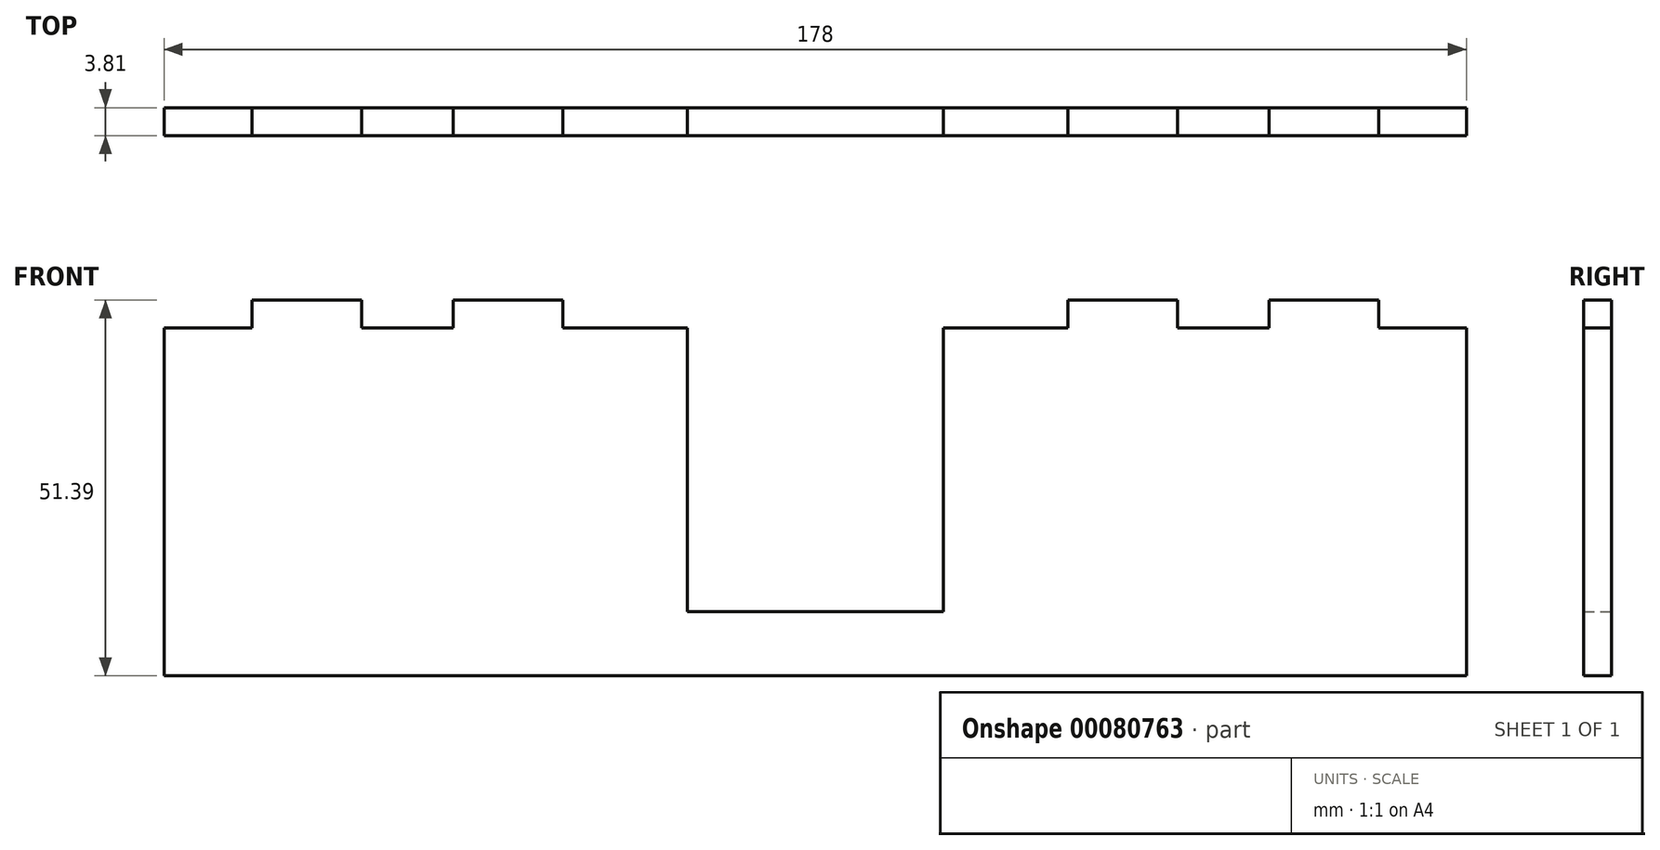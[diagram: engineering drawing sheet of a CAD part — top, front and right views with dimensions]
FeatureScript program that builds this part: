
annotation { "Feature Type Name" : "Feature", "Feature Type Description" : "" }
export const myFeature = defineFeature(function(context is Context, id is Id, definition is map)
    precondition{}
    {
        {
            var Q0;
            Q0=qCreatedBy(makeId("Front.planeOp"),FACE);
            var sketch = newSketch(context, id + "F0", { "sketchPlane" : qUnion([Q0])});
            skLineSegment(sketch, "E0.bottom", {"start": v(89, 23.79) * mm, "end": v(-89, 23.8) * mm});
            skLineSegment(sketch, "E0.top", {"start": v(89, -23.8) * mm, "end": v(-89, -23.79) * mm});
            skLineSegment(sketch, "E0.left", {"start": v(89, 23.79) * mm, "end": v(89, -23.79) * mm});
            skLineSegment(sketch, "E0.right", {"start": v(-89, 23.8) * mm, "end": v(-89, -23.79) * mm});
            skPoint(sketch, "E0.middle", {"position": v(0, 0) * mm});
            skLineSegment(sketch, "E1", {"start": v(0, 23.79) * mm, "end": v(0, -23.8) * mm});
            skLineSegment(sketch, "E2", {"start": v(-77, 23.8) * mm, "end": v(-77, 27.6) * mm});
            skLineSegment(sketch, "E3", {"start": v(-62, 23.8) * mm, "end": v(-62, 27.6) * mm});
            skLineSegment(sketch, "E4", {"start": v(-62, 27.6) * mm, "end": v(-77, 27.6) * mm});
            skLineSegment(sketch, "E5", {"start": v(-49.5, 23.8) * mm, "end": v(-49.5, 27.6) * mm});
            skLineSegment(sketch, "E6", {"start": v(-49.5, 27.6) * mm, "end": v(-34.5, 27.6) * mm});
            skLineSegment(sketch, "E7", {"start": v(-34.5, 27.6) * mm, "end": v(-34.5, 23.79) * mm});
            skLineSegment(sketch, "E8.MirrorCS", {"start": v(49.5, 27.6) * mm, "end": v(34.5, 27.6) * mm});
            skLineSegment(sketch, "E9.MirrorCS", {"start": v(49.5, 23.8) * mm, "end": v(49.5, 27.6) * mm});
            skLineSegment(sketch, "E10.MirrorCS", {"start": v(34.5, 27.6) * mm, "end": v(34.5, 23.79) * mm});
            skLineSegment(sketch, "E11.MirrorCS", {"start": v(62, 27.6) * mm, "end": v(77, 27.6) * mm});
            skLineSegment(sketch, "E12.MirrorCS", {"start": v(77, 23.8) * mm, "end": v(77, 27.6) * mm});
            skLineSegment(sketch, "E13.MirrorCS", {"start": v(62, 23.8) * mm, "end": v(62, 27.6) * mm});
            skLineSegment(sketch, "E14", {"start": v(-17.5, 23.79) * mm, "end": v(-17.5, 0) * mm});
            skLineSegment(sketch, "E15", {"start": v(-17.5, 0) * mm, "end": v(0, 0) * mm});
            skLineSegment(sketch, "E16.MirrorCS", {"start": v(17.5, 23.79) * mm, "end": v(17.5, 0) * mm});
            skLineSegment(sketch, "E17.MirrorCS", {"start": v(17.5, 0) * mm, "end": v(0, 0) * mm});
            skLineSegment(sketch, "E18", {"start": v(-17.5, 0) * mm, "end": v(-17.5, -15) * mm});
            skLineSegment(sketch, "E19", {"start": v(-17.5, -15) * mm, "end": v(17.5, -15) * mm});
            skLineSegment(sketch, "E20", {"start": v(17.5, -15) * mm, "end": v(17.5, 0) * mm});
            skSolve(sketch);
        }
        {
            var Q0;
            Q0=makeQuery(id+"F0.imprint","IMPRINT",FACE,{"disambiguationData":[TD([[makeQuery(id+"F0.imprint","IMPRINT",EDGE,{"derivedFrom":sQuery(id+"F0.wireOp",EDGE,"E0.bottom")}),1.0]])]});
            var Q1;
            {var subQ0=sQuery(id+"F0.wireOp",EDGE,"E2");Q1=makeQuery(id+"F0.imprint","IMPRINT",FACE,{"disambiguationData":[TD([[makeQuery(id+"F0.imprint","IMPRINT",EDGE,{"derivedFrom":subQ0}),-1.0]])]});}
            var Q2;
            {var subQ0=sQuery(id+"F0.wireOp",EDGE,"E5");Q2=makeQuery(id+"F0.imprint","IMPRINT",FACE,{"disambiguationData":[TD([[makeQuery(id+"F0.imprint","IMPRINT",EDGE,{"derivedFrom":subQ0}),-1.0]])]});}
            var Q3;
            Q3=makeQuery(id+"F0.imprint","IMPRINT",FACE,{"disambiguationData":[TD([[makeQuery(id+"F0.imprint","IMPRINT",EDGE,{"derivedFrom":sQuery(id+"F0.wireOp",EDGE,"E8.MirrorCS")}),1.0]])]});
            var Q4;
            Q4=makeQuery(id+"F0.imprint","IMPRINT",FACE,{"disambiguationData":[TD([[makeQuery(id+"F0.imprint","IMPRINT",EDGE,{"derivedFrom":sQuery(id+"F0.wireOp",EDGE,"E11.MirrorCS")}),-1.0]])]});
            extrude(context, id + "F1", {"entities" : qUnion([Q0, Q1, Q2, Q3, Q4]), "depth" : 3.8 * mm});
        }
    });
